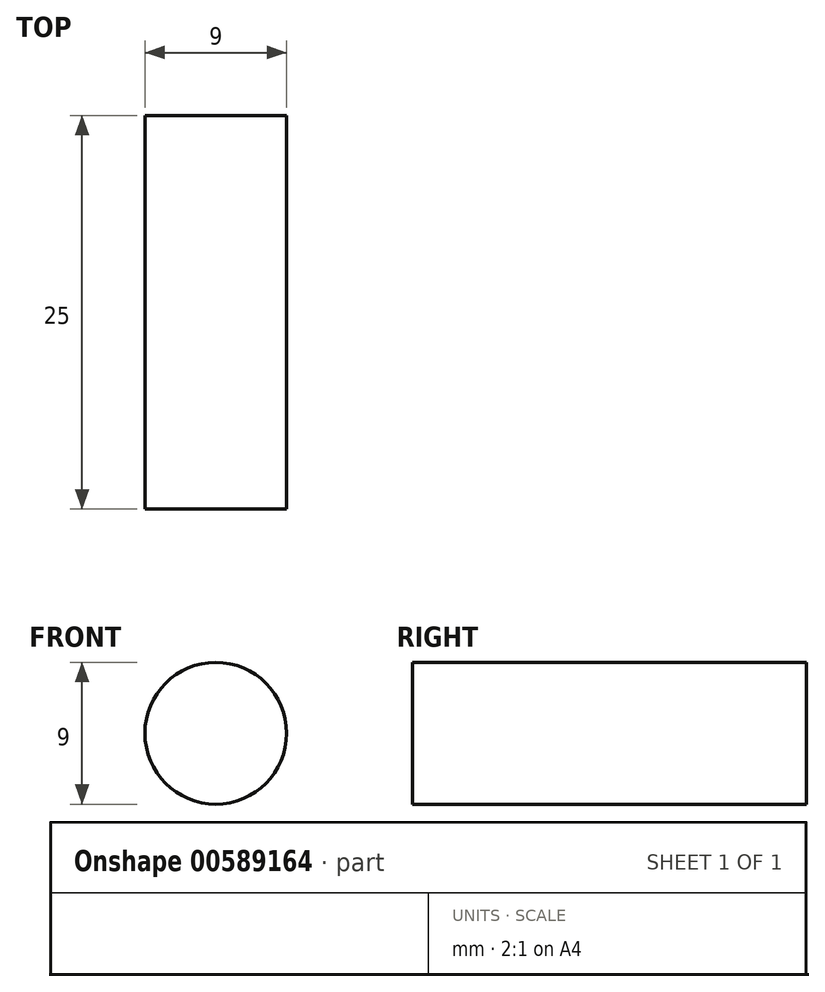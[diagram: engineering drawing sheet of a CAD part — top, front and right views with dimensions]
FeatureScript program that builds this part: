
annotation { "Feature Type Name" : "Feature", "Feature Type Description" : "" }
export const myFeature = defineFeature(function(context is Context, id is Id, definition is map)
    precondition{}
    {
        {
            var Q0;
            Q0=qCreatedBy(makeId("Front.planeOp"),FACE);
            var sketch = newSketch(context, id + "F0", { "sketchPlane" : qUnion([Q0])});
            skCircle(sketch, "E0", {"center": v(0, 0) * mm, "radius": 4.5 * mm});
            skSolve(sketch);
        }
        {
            var Q0;
            Q0 = qSketchRegion(id + "F0", true);
            extrude(context, id + "F1", {"entities" : qUnion([Q0]), "depth" : 25 * mm, "offsetDistance" : 25 * mm});
        }
    });
